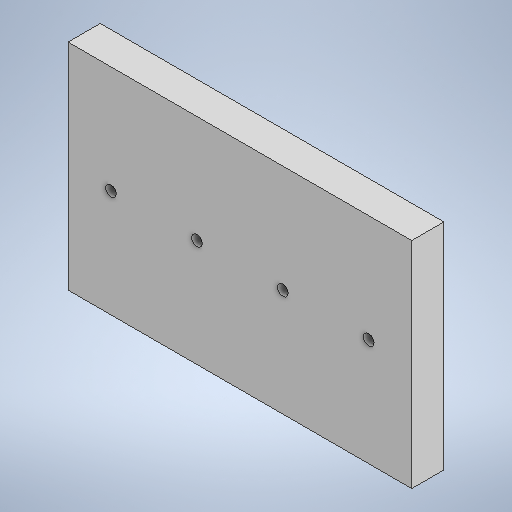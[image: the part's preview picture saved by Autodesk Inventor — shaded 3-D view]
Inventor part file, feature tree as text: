
AUTODESK INVENTOR PART (.ipt)
format: ipt  version: 2025 (Build 290162010, 162A)  size: 219,136 bytes
history: native  units: in
note: dims shown in document units (in); Inventor stores cm internally (conversion verified against a paired STEP export)
features: extrude x2, sketch x2
ambient origin geometry x8: Origin, YZ Plane, XZ Plane, XY Plane, X Axis, Y Axis, Z Axis, Center Point
bodies: Solid1 (feature_tree)
feature tree (4):
  extrude  "Extrusion1"  Depth=5.0in
  extrude  "Extrusion2"  Depth=0.75in
  sketch  "Sketch1"  dims[d0=8.0in d1=5.0in]
  sketch  "Sketch2"  dims[d2=0.25in d3=0.25in d4=0.25in d5=0.25in d6=1.0in d7=3.0in d8=5.0in d9=7.0in d10=0.75in d11=0.0in d12=0.25in d13=0.25in d14=0.25in d15=0.25in d17=2.5in d18=2.5in d19=1.0in d20=3.0in d21=5.0in d22=7.0in d23=0.75in d24=0.0in]
